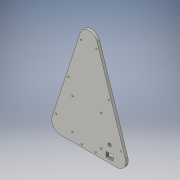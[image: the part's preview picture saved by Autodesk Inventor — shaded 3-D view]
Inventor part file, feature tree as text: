
AUTODESK INVENTOR PART (.ipt)
format: ipt  version: 2016 (Build 200138000, 138)  size: 177,664 bytes
history: native  units: in
note: dims shown in document units (in); Inventor stores cm internally (conversion verified against a paired STEP export)
features: fillet x4, sketch x3, extrude x3, plane x1
ambient origin geometry x8: Origin, YZ Plane, XZ Plane, XY Plane, X Axis, Y Axis, Z Axis, Center Point
bodies: Body1 (feature_tree)
feature tree (11):
  sketch  "Sketch1"  dims[d39=1.25in d40=1.25in d41=1.0in d42=1.0in d43=1.0in d44=0.4in d45=0.4in d46=0.05in d47=0.05in d48=0.4in d49=0.4in d50=0.1in d51=0.1in d52=0.1in d53=0.1in d71=2.2in]
  plane  "Work Plane1"
  sketch  "Sketch2"  dims[d73=2.05in d74=0.1in d75=0.1in d76=0.1in d77=0.1in d80=2.05in]
  extrude  "Extrusion8"  Depth=0.05in
  extrude  "Extrusion10"  Depth=0.1in
  fillet  "Fillet1"  Radius=0.1in
  fillet  "Fillet2"  Radius=0.1in
  fillet  "Fillet3"  Radius=0.1in
  fillet  "Fillet4"  Radius=2.05in
  extrude  "Extrusion11"  Depth=0.025in
  sketch  "Sketch3"  dims[d81=0.6in d82=1.15in d91=0.5in d92=0.5in d93=0.18in d94=0.0in d97=0.09in d98=0.5in d99=0.35in d100=1.0in d101=0.0in d102=0.025in d103=0.025in d104=0.025in d105=0.025in d106=0.22in d107=1.0in d108=0.0in d109=1.4834in]
